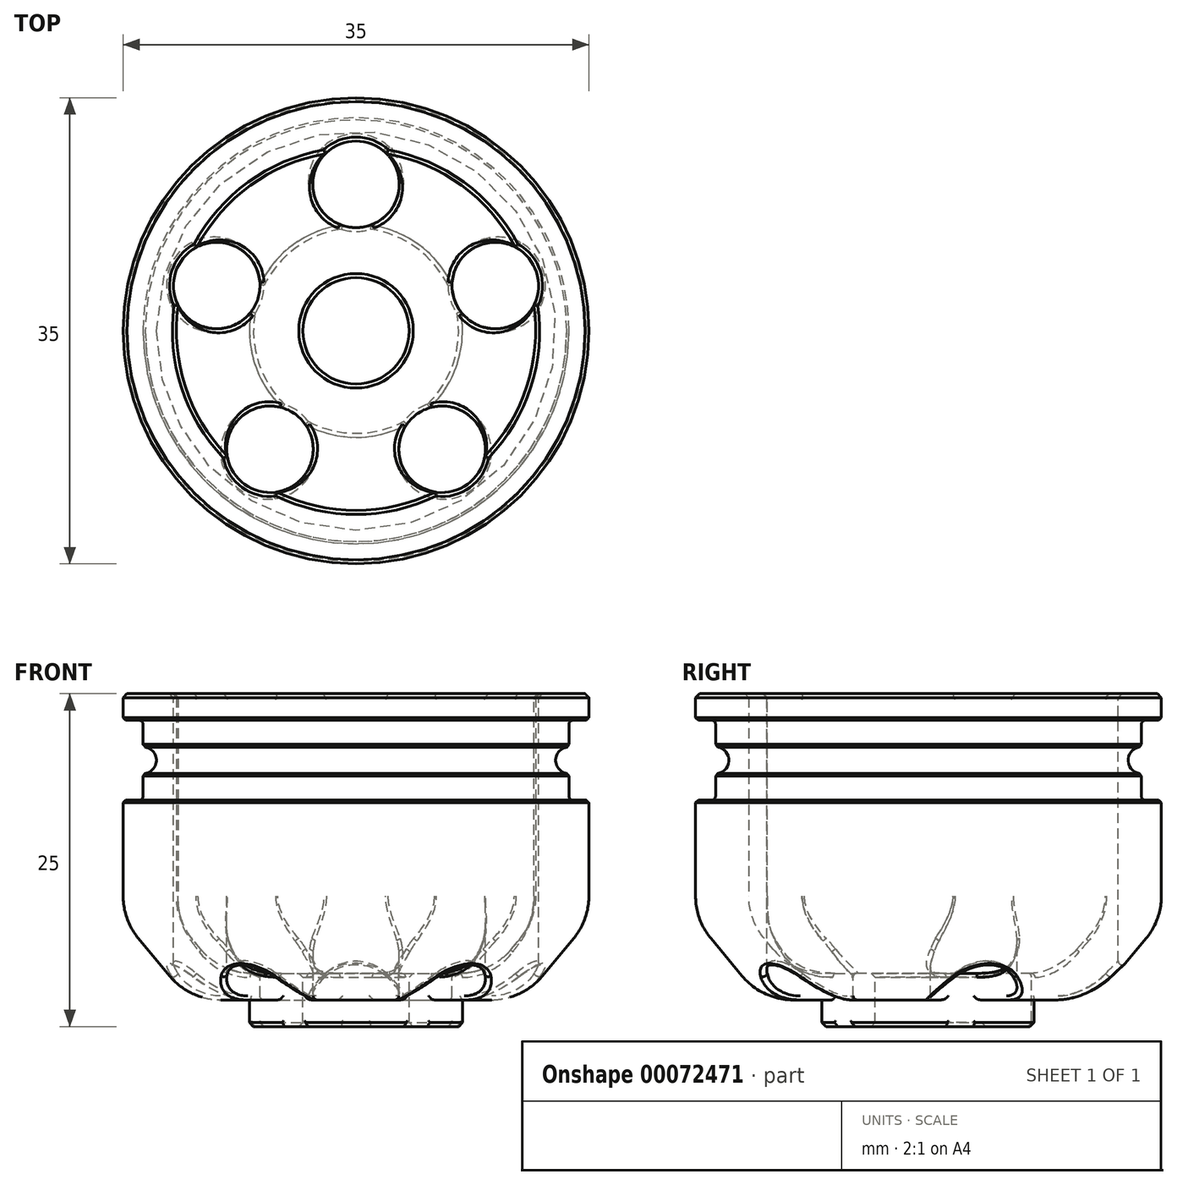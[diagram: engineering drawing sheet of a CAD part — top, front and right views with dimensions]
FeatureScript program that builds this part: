
annotation { "Feature Type Name" : "Feature", "Feature Type Description" : "" }
export const myFeature = defineFeature(function(context is Context, id is Id, definition is map)
    precondition{}
    {
        {
            var Q0;
            Q0=qCreatedBy(makeId("Front.planeOp"),FACE);
            var sketch = newSketch(context, id + "F0", { "sketchPlane" : qUnion([Q0])});
            skLineSegment(sketch, "E0", {"start": v(0, 0) * mm, "end": v(0, 25.98) * mm, "construction": true});
            skLineSegment(sketch, "E1.bottom", {"start": v(0, 0) * mm, "end": v(-8, 0) * mm});
            skLineSegment(sketch, "E1.left", {"start": v(0, 0) * mm, "end": v(0, 2) * mm});
            skLineSegment(sketch, "E1.right", {"start": v(-8, 0) * mm, "end": v(-8, 2) * mm});
            skLineSegment(sketch, "E2.top", {"start": v(0, 4) * mm, "end": v(-10.16, 4) * mm});
            skLineSegment(sketch, "E2.left", {"start": v(0, 2) * mm, "end": v(0, 4) * mm});
            skLineSegment(sketch, "E2.right", {"start": v(-12.5, 2) * mm, "end": v(-12.5, 2) * mm});
            skLineSegment(sketch, "E3", {"start": v(0, 25) * mm, "end": v(-17.5, 25) * mm, "construction": true});
            skLineSegment(sketch, "E4", {"start": v(-17.5, 25) * mm, "end": v(-17.5, 0) * mm, "construction": true});
            skLineSegment(sketch, "E5.bottom", {"start": v(-17.5, 25) * mm, "end": v(-13.5, 25) * mm});
            skLineSegment(sketch, "E5.left", {"start": v(-17.5, 25) * mm, "end": v(-17.5, 23) * mm});
            skLineSegment(sketch, "E5.right", {"start": v(-13.5, 25) * mm, "end": v(-13.5, 8) * mm});
            skLineSegment(sketch, "E6.bottom", {"start": v(-17.5, 23) * mm, "end": v(-16, 23) * mm});
            skLineSegment(sketch, "E6.top", {"start": v(-17.5, 17) * mm, "end": v(-16, 17) * mm});
            skLineSegment(sketch, "E6.right", {"start": v(-16, 23) * mm, "end": v(-16, 21) * mm});
            skLineSegment(sketch, "E7", {"start": v(-17.5, 17) * mm, "end": v(-17.5, 8) * mm});
            skArc(sketch, "E8", {"start": v(-16, 19) * mm, "mid": v(-15, 20) * mm, "end": v(-16, 21) * mm});
            skLineSegment(sketch, "E9", {"start": v(-16, 19) * mm, "end": v(-16, 17) * mm});
            skLineSegment(sketch, "E10", {"start": v(-17.5, 8) * mm, "end": v(-12.5, 2) * mm});
            skLineSegment(sketch, "E11", {"start": v(-13.5, 8) * mm, "end": v(-10.16, 4) * mm});
            skLineSegment(sketch, "E12", {"start": v(-8, 2) * mm, "end": v(-12.5, 2) * mm});
            skSolve(sketch);
        }
        {
            var Q0;
            Q0=makeQuery(id+"F0.imprint","IMPRINT",FACE,{"disambiguationData":[TD([[makeQuery(id+"F0.imprint","IMPRINT",EDGE,{"derivedFrom":sQuery(id+"F0.wireOp",EDGE,"E1.bottom")}),-1.0]])]});
            var Q1;
            Q1=sQuery(id+"F0.wireOp",EDGE,"E0");
            revolve(context, id + "F1", {"entities" : qUnion([Q0]), "axis" : qUnion([Q1]), "revolveType" : RevolveType.FULL});
        }
        {
            var Q0;
            Q0=makeQuery(id+"F1.opRevolve","SWEPT_FACE",FACE,{"disambiguationData":[OSD([sQuery(id+"F0.wireOp",EDGE,"E5.bottom")])]});
            var sketch = newSketch(context, id + "F2", { "sketchPlane" : qUnion([Q0])});
            skCircle(sketch, "E13", {"center": v(0, 0) * mm, "radius": 4 * mm});
            skLineSegment(sketch, "E14", {"start": v(0, 0) * mm, "end": v(0, 11) * mm, "construction": true});
            skCircle(sketch, "E15", {"center": v(0, 0) * mm, "radius": 15 * mm, "construction": true});
            skCircle(sketch, "E16", {"center": v(0, 11) * mm, "radius": 3.25 * mm});
            skCircle(sketch, "E17.1.0", {"center": v(-10.46, 3.4) * mm, "radius": 3.25 * mm});
            skCircle(sketch, "E17.2.0", {"center": v(-6.47, -8.9) * mm, "radius": 3.25 * mm});
            skCircle(sketch, "E17.3.0", {"center": v(6.47, -8.9) * mm, "radius": 3.25 * mm});
            skCircle(sketch, "E17.4.0", {"center": v(10.46, 3.4) * mm, "radius": 3.25 * mm});
            skSolve(sketch);
        }
        {
            var Q0;
            {var subQ0=sQuery(id+"F2.wireOp",EDGE,"E16");var subQ1=makeQuery(id+"F1.opRevolve","SWEPT_EDGE",EDGE,{"disambiguationData":[OSD([sQuery(id+"F0.wireOp",EDGE,"E5.bottom"),sQuery(id+"F0.wireOp",EDGE,"E5.right")])]});var subQ2=makeQuery(id+"F2.imprint","INTERSECT",VERTEX,{"disambiguationData":[OD(0.0)],"derivedFrom":[subQ1,subQ0]});Q0=makeQuery(id+"F2.imprint","IMPRINT",FACE,{"disambiguationData":[TD([[makeQuery(id+"F2.imprint","IMPRINT",EDGE,{"disambiguationData":[TD([[subQ2,-1.0]])],"derivedFrom":subQ0}),1.0]])]});}
            var Q1;
            {var subQ0=sQuery(id+"F2.wireOp",EDGE,"E16");var subQ1=makeQuery(id+"F1.opRevolve","SWEPT_EDGE",EDGE,{"disambiguationData":[OSD([sQuery(id+"F0.wireOp",EDGE,"E5.bottom"),sQuery(id+"F0.wireOp",EDGE,"E5.right")])]});var subQ2=makeQuery(id+"F2.imprint","INTERSECT",VERTEX,{"disambiguationData":[OD(0.0)],"derivedFrom":[subQ1,subQ0]});Q1=makeQuery(id+"F2.imprint","IMPRINT",FACE,{"disambiguationData":[TD([[makeQuery(id+"F2.imprint","IMPRINT",EDGE,{"disambiguationData":[TD([[subQ2,1.0]])],"derivedFrom":subQ0}),1.0]])]});}
            var Q2;
            {var subQ0=sQuery(id+"F2.wireOp",EDGE,"E17.1.0");var subQ1=makeQuery(id+"F1.opRevolve","SWEPT_EDGE",EDGE,{"disambiguationData":[OSD([sQuery(id+"F0.wireOp",EDGE,"E5.bottom"),sQuery(id+"F0.wireOp",EDGE,"E5.right")])]});var subQ2=makeQuery(id+"F2.imprint","INTERSECT",VERTEX,{"disambiguationData":[OD(0.0)],"derivedFrom":[subQ1,subQ0]});Q2=makeQuery(id+"F2.imprint","IMPRINT",FACE,{"disambiguationData":[TD([[makeQuery(id+"F2.imprint","IMPRINT",EDGE,{"disambiguationData":[TD([[subQ2,-1.0]])],"derivedFrom":subQ0}),1.0]])]});}
            var Q3;
            {var subQ0=sQuery(id+"F2.wireOp",EDGE,"E17.1.0");var subQ1=makeQuery(id+"F1.opRevolve","SWEPT_EDGE",EDGE,{"disambiguationData":[OSD([sQuery(id+"F0.wireOp",EDGE,"E5.bottom"),sQuery(id+"F0.wireOp",EDGE,"E5.right")])]});var subQ2=makeQuery(id+"F2.imprint","INTERSECT",VERTEX,{"disambiguationData":[OD(0.0)],"derivedFrom":[subQ1,subQ0]});Q3=makeQuery(id+"F2.imprint","IMPRINT",FACE,{"disambiguationData":[TD([[makeQuery(id+"F2.imprint","IMPRINT",EDGE,{"disambiguationData":[TD([[subQ2,1.0]])],"derivedFrom":subQ0}),1.0]])]});}
            var Q4;
            {var subQ0=sQuery(id+"F2.wireOp",EDGE,"E17.2.0");var subQ1=makeQuery(id+"F1.opRevolve","SWEPT_EDGE",EDGE,{"disambiguationData":[OSD([sQuery(id+"F0.wireOp",EDGE,"E5.bottom"),sQuery(id+"F0.wireOp",EDGE,"E5.right")])]});var subQ2=makeQuery(id+"F2.imprint","INTERSECT",VERTEX,{"disambiguationData":[OD(0.0)],"derivedFrom":[subQ1,subQ0]});Q4=makeQuery(id+"F2.imprint","IMPRINT",FACE,{"disambiguationData":[TD([[makeQuery(id+"F2.imprint","IMPRINT",EDGE,{"disambiguationData":[TD([[subQ2,1.0]])],"derivedFrom":subQ0}),1.0]])]});}
            var Q5;
            {var subQ0=sQuery(id+"F2.wireOp",EDGE,"E17.2.0");var subQ1=makeQuery(id+"F1.opRevolve","SWEPT_EDGE",EDGE,{"disambiguationData":[OSD([sQuery(id+"F0.wireOp",EDGE,"E5.bottom"),sQuery(id+"F0.wireOp",EDGE,"E5.right")])]});var subQ2=makeQuery(id+"F2.imprint","INTERSECT",VERTEX,{"disambiguationData":[OD(0.0)],"derivedFrom":[subQ1,subQ0]});Q5=makeQuery(id+"F2.imprint","IMPRINT",FACE,{"disambiguationData":[TD([[makeQuery(id+"F2.imprint","IMPRINT",EDGE,{"disambiguationData":[TD([[subQ2,-1.0]])],"derivedFrom":subQ0}),1.0]])]});}
            var Q6;
            {var subQ0=sQuery(id+"F2.wireOp",EDGE,"E17.3.0");var subQ1=makeQuery(id+"F1.opRevolve","SWEPT_EDGE",EDGE,{"disambiguationData":[OSD([sQuery(id+"F0.wireOp",EDGE,"E5.bottom"),sQuery(id+"F0.wireOp",EDGE,"E5.right")])]});var subQ2=makeQuery(id+"F2.imprint","INTERSECT",VERTEX,{"disambiguationData":[OD(0.0)],"derivedFrom":[subQ1,subQ0]});Q6=makeQuery(id+"F2.imprint","IMPRINT",FACE,{"disambiguationData":[TD([[makeQuery(id+"F2.imprint","IMPRINT",EDGE,{"disambiguationData":[TD([[subQ2,1.0]])],"derivedFrom":subQ0}),1.0]])]});}
            var Q7;
            {var subQ0=sQuery(id+"F2.wireOp",EDGE,"E17.3.0");var subQ1=makeQuery(id+"F1.opRevolve","SWEPT_EDGE",EDGE,{"disambiguationData":[OSD([sQuery(id+"F0.wireOp",EDGE,"E5.bottom"),sQuery(id+"F0.wireOp",EDGE,"E5.right")])]});var subQ2=makeQuery(id+"F2.imprint","INTERSECT",VERTEX,{"disambiguationData":[OD(0.0)],"derivedFrom":[subQ1,subQ0]});Q7=makeQuery(id+"F2.imprint","IMPRINT",FACE,{"disambiguationData":[TD([[makeQuery(id+"F2.imprint","IMPRINT",EDGE,{"disambiguationData":[TD([[subQ2,-1.0]])],"derivedFrom":subQ0}),1.0]])]});}
            var Q8;
            {var subQ0=sQuery(id+"F2.wireOp",EDGE,"E17.4.0");var subQ1=makeQuery(id+"F1.opRevolve","SWEPT_EDGE",EDGE,{"disambiguationData":[OSD([sQuery(id+"F0.wireOp",EDGE,"E5.bottom"),sQuery(id+"F0.wireOp",EDGE,"E5.right")])]});var subQ2=makeQuery(id+"F2.imprint","INTERSECT",VERTEX,{"disambiguationData":[OD(0.0)],"derivedFrom":[subQ1,subQ0]});Q8=makeQuery(id+"F2.imprint","IMPRINT",FACE,{"disambiguationData":[TD([[makeQuery(id+"F2.imprint","IMPRINT",EDGE,{"disambiguationData":[TD([[subQ2,1.0]])],"derivedFrom":subQ0}),1.0]])]});}
            var Q9;
            {var subQ0=sQuery(id+"F2.wireOp",EDGE,"E17.4.0");var subQ1=makeQuery(id+"F1.opRevolve","SWEPT_EDGE",EDGE,{"disambiguationData":[OSD([sQuery(id+"F0.wireOp",EDGE,"E5.bottom"),sQuery(id+"F0.wireOp",EDGE,"E5.right")])]});var subQ2=makeQuery(id+"F2.imprint","INTERSECT",VERTEX,{"disambiguationData":[OD(0.0)],"derivedFrom":[subQ1,subQ0]});Q9=makeQuery(id+"F2.imprint","IMPRINT",FACE,{"disambiguationData":[TD([[makeQuery(id+"F2.imprint","IMPRINT",EDGE,{"disambiguationData":[TD([[subQ2,-1.0]])],"derivedFrom":subQ0}),1.0]])]});}
            var Q10;
            Q10=makeQuery(id+"F2.imprint","IMPRINT",FACE,{"disambiguationData":[TD([[makeQuery(id+"F2.imprint","IMPRINT",EDGE,{"derivedFrom":sQuery(id+"F2.wireOp",EDGE,"E13")}),1.0]])]});
            extrude(context, id + "F3", {"entities" : qUnion([Q0, Q1, Q2, Q3, Q4, Q5, Q6, Q7, Q8, Q9, Q10]), "operationType" : NewBodyOperationType.REMOVE, "endBound" : BoundingType.THROUGH_ALL, "oppositeDirection" : true, "depth" : 25 * mm});
        }
        {
            var Q0;
            Q0=makeQuery(id+"F1.opRevolve","SWEPT_FACE",FACE,{"disambiguationData":[OSD([sQuery(id+"F0.wireOp",EDGE,"E5.bottom")])]});
            chamfer(context, id + "F4", {"entities" : qUnion([Q0]), "width" : .3 * mm, "tangentPropagation" : true});
        }
        {
            var Q0;
            Q0=makeQuery(id+"F3.boolean.opBoolean","COPY",FACE,{"derivedFrom":makeQuery(id+"F3.opExtrude","SWEPT_FACE",FACE,{"disambiguationData":[OSD([sQuery(id+"F2.wireOp",EDGE,"E13")])]})});
            var Q1;
            Q1=makeQuery(id+"F1.opRevolve","SWEPT_FACE",FACE,{"disambiguationData":[OSD([sQuery(id+"F0.wireOp",EDGE,"E1.bottom")])]});
            chamfer(context, id + "F5", {"entities" : qUnion([Q0, Q1]), "width" : .3 * mm, "tangentPropagation" : true});
        }
        {
            var Q0;
            {var subQ0=sQuery(id+"F0.wireOp",EDGE,"E10");var subQ1=sQuery(id+"F0.wireOp",EDGE,"E12");Q0=makeQuery(id+"F3.boolean.opBoolean","SPLIT",EDGE,{"disambiguationData":[TD([makeQuery(id+"F1.opRevolve","SWEPT_FACE",FACE,{"disambiguationData":[OSD([subQ0])]}),makeQuery(id+"F1.opRevolve","SWEPT_FACE",FACE,{"disambiguationData":[OSD([subQ1])]}),makeQuery(id+"F3.opExtrude","SWEPT_FACE",FACE,{"disambiguationData":[OSD([sQuery(id+"F2.wireOp",EDGE,"E17.2.0")])]}),makeQuery(id+"F3.opExtrude","SWEPT_FACE",FACE,{"disambiguationData":[OSD([sQuery(id+"F2.wireOp",EDGE,"E17.3.0")])]})])],"derivedFrom":makeQuery(id+"F1.opRevolve","SWEPT_EDGE",EDGE,{"disambiguationData":[OSD([subQ0,subQ1])]})});}
            var Q1;
            {var subQ0=sQuery(id+"F0.wireOp",EDGE,"E10");var subQ1=sQuery(id+"F0.wireOp",EDGE,"E12");Q1=makeQuery(id+"F3.boolean.opBoolean","SPLIT",EDGE,{"disambiguationData":[TD([makeQuery(id+"F1.opRevolve","SWEPT_FACE",FACE,{"disambiguationData":[OSD([subQ0])]}),makeQuery(id+"F1.opRevolve","SWEPT_FACE",FACE,{"disambiguationData":[OSD([subQ1])]}),makeQuery(id+"F3.opExtrude","SWEPT_FACE",FACE,{"disambiguationData":[OSD([sQuery(id+"F2.wireOp",EDGE,"E17.3.0")])]}),makeQuery(id+"F3.opExtrude","SWEPT_FACE",FACE,{"disambiguationData":[OSD([sQuery(id+"F2.wireOp",EDGE,"E17.4.0")])]})])],"derivedFrom":makeQuery(id+"F1.opRevolve","SWEPT_EDGE",EDGE,{"disambiguationData":[OSD([subQ0,subQ1])]})});}
            var Q2;
            {var subQ0=sQuery(id+"F0.wireOp",EDGE,"E10");var subQ1=sQuery(id+"F0.wireOp",EDGE,"E12");Q2=makeQuery(id+"F3.boolean.opBoolean","SPLIT",EDGE,{"disambiguationData":[TD([makeQuery(id+"F1.opRevolve","SWEPT_FACE",FACE,{"disambiguationData":[OSD([subQ0])]}),makeQuery(id+"F1.opRevolve","SWEPT_FACE",FACE,{"disambiguationData":[OSD([subQ1])]}),makeQuery(id+"F3.opExtrude","SWEPT_FACE",FACE,{"disambiguationData":[OSD([sQuery(id+"F2.wireOp",EDGE,"E16")])]}),makeQuery(id+"F3.opExtrude","SWEPT_FACE",FACE,{"disambiguationData":[OSD([sQuery(id+"F2.wireOp",EDGE,"E17.4.0")])]})])],"derivedFrom":makeQuery(id+"F1.opRevolve","SWEPT_EDGE",EDGE,{"disambiguationData":[OSD([subQ0,subQ1])]})});}
            var Q3;
            {var subQ0=sQuery(id+"F0.wireOp",EDGE,"E10");var subQ1=sQuery(id+"F0.wireOp",EDGE,"E12");Q3=makeQuery(id+"F3.boolean.opBoolean","SPLIT",EDGE,{"disambiguationData":[TD([makeQuery(id+"F1.opRevolve","SWEPT_FACE",FACE,{"disambiguationData":[OSD([subQ0])]}),makeQuery(id+"F1.opRevolve","SWEPT_FACE",FACE,{"disambiguationData":[OSD([subQ1])]}),makeQuery(id+"F3.opExtrude","SWEPT_FACE",FACE,{"disambiguationData":[OSD([sQuery(id+"F2.wireOp",EDGE,"E16")])]}),makeQuery(id+"F3.opExtrude","SWEPT_FACE",FACE,{"disambiguationData":[OSD([sQuery(id+"F2.wireOp",EDGE,"E17.1.0")])]})])],"derivedFrom":makeQuery(id+"F1.opRevolve","SWEPT_EDGE",EDGE,{"disambiguationData":[OSD([subQ0,subQ1])]})});}
            var Q4;
            {var subQ0=sQuery(id+"F0.wireOp",EDGE,"E10");var subQ1=sQuery(id+"F0.wireOp",EDGE,"E12");Q4=makeQuery(id+"F3.boolean.opBoolean","SPLIT",EDGE,{"disambiguationData":[TD([makeQuery(id+"F1.opRevolve","SWEPT_FACE",FACE,{"disambiguationData":[OSD([subQ0])]}),makeQuery(id+"F1.opRevolve","SWEPT_FACE",FACE,{"disambiguationData":[OSD([subQ1])]}),makeQuery(id+"F3.opExtrude","SWEPT_FACE",FACE,{"disambiguationData":[OSD([sQuery(id+"F2.wireOp",EDGE,"E17.1.0")])]}),makeQuery(id+"F3.opExtrude","SWEPT_FACE",FACE,{"disambiguationData":[OSD([sQuery(id+"F2.wireOp",EDGE,"E17.2.0")])]})])],"derivedFrom":makeQuery(id+"F1.opRevolve","SWEPT_EDGE",EDGE,{"disambiguationData":[OSD([subQ0,subQ1])]})});}
            var Q5;
            {var subQ0=sQuery(id+"F0.wireOp",EDGE,"E2.top");var subQ1=sQuery(id+"F0.wireOp",EDGE,"E11");Q5=makeQuery(id+"F3.boolean.opBoolean","SPLIT",EDGE,{"disambiguationData":[TD([makeQuery(id+"F1.opRevolve","SWEPT_FACE",FACE,{"disambiguationData":[OSD([subQ0])]}),makeQuery(id+"F1.opRevolve","SWEPT_FACE",FACE,{"disambiguationData":[OSD([subQ1])]}),makeQuery(id+"F3.opExtrude","SWEPT_FACE",FACE,{"disambiguationData":[OSD([sQuery(id+"F2.wireOp",EDGE,"E17.2.0")])]}),makeQuery(id+"F3.opExtrude","SWEPT_FACE",FACE,{"disambiguationData":[OSD([sQuery(id+"F2.wireOp",EDGE,"E17.3.0")])]})])],"derivedFrom":makeQuery(id+"F1.opRevolve","SWEPT_EDGE",EDGE,{"disambiguationData":[OSD([subQ0,subQ1])]})});}
            var Q6;
            {var subQ0=sQuery(id+"F0.wireOp",EDGE,"E2.top");var subQ1=sQuery(id+"F0.wireOp",EDGE,"E11");Q6=makeQuery(id+"F3.boolean.opBoolean","SPLIT",EDGE,{"disambiguationData":[TD([makeQuery(id+"F1.opRevolve","SWEPT_FACE",FACE,{"disambiguationData":[OSD([subQ0])]}),makeQuery(id+"F1.opRevolve","SWEPT_FACE",FACE,{"disambiguationData":[OSD([subQ1])]}),makeQuery(id+"F3.opExtrude","SWEPT_FACE",FACE,{"disambiguationData":[OSD([sQuery(id+"F2.wireOp",EDGE,"E17.3.0")])]}),makeQuery(id+"F3.opExtrude","SWEPT_FACE",FACE,{"disambiguationData":[OSD([sQuery(id+"F2.wireOp",EDGE,"E17.4.0")])]})])],"derivedFrom":makeQuery(id+"F1.opRevolve","SWEPT_EDGE",EDGE,{"disambiguationData":[OSD([subQ0,subQ1])]})});}
            var Q7;
            {var subQ0=sQuery(id+"F0.wireOp",EDGE,"E2.top");var subQ1=sQuery(id+"F0.wireOp",EDGE,"E11");Q7=makeQuery(id+"F3.boolean.opBoolean","SPLIT",EDGE,{"disambiguationData":[TD([makeQuery(id+"F1.opRevolve","SWEPT_FACE",FACE,{"disambiguationData":[OSD([subQ0])]}),makeQuery(id+"F1.opRevolve","SWEPT_FACE",FACE,{"disambiguationData":[OSD([subQ1])]}),makeQuery(id+"F3.opExtrude","SWEPT_FACE",FACE,{"disambiguationData":[OSD([sQuery(id+"F2.wireOp",EDGE,"E17.1.0")])]}),makeQuery(id+"F3.opExtrude","SWEPT_FACE",FACE,{"disambiguationData":[OSD([sQuery(id+"F2.wireOp",EDGE,"E17.2.0")])]})])],"derivedFrom":makeQuery(id+"F1.opRevolve","SWEPT_EDGE",EDGE,{"disambiguationData":[OSD([subQ0,subQ1])]})});}
            var Q8;
            {var subQ0=sQuery(id+"F0.wireOp",EDGE,"E2.top");var subQ1=sQuery(id+"F0.wireOp",EDGE,"E11");Q8=makeQuery(id+"F3.boolean.opBoolean","SPLIT",EDGE,{"disambiguationData":[TD([makeQuery(id+"F1.opRevolve","SWEPT_FACE",FACE,{"disambiguationData":[OSD([subQ0])]}),makeQuery(id+"F1.opRevolve","SWEPT_FACE",FACE,{"disambiguationData":[OSD([subQ1])]}),makeQuery(id+"F3.opExtrude","SWEPT_FACE",FACE,{"disambiguationData":[OSD([sQuery(id+"F2.wireOp",EDGE,"E16")])]}),makeQuery(id+"F3.opExtrude","SWEPT_FACE",FACE,{"disambiguationData":[OSD([sQuery(id+"F2.wireOp",EDGE,"E17.1.0")])]})])],"derivedFrom":makeQuery(id+"F1.opRevolve","SWEPT_EDGE",EDGE,{"disambiguationData":[OSD([subQ0,subQ1])]})});}
            var Q9;
            {var subQ0=sQuery(id+"F0.wireOp",EDGE,"E2.top");var subQ1=sQuery(id+"F0.wireOp",EDGE,"E11");Q9=makeQuery(id+"F3.boolean.opBoolean","SPLIT",EDGE,{"disambiguationData":[TD([makeQuery(id+"F1.opRevolve","SWEPT_FACE",FACE,{"disambiguationData":[OSD([subQ0])]}),makeQuery(id+"F1.opRevolve","SWEPT_FACE",FACE,{"disambiguationData":[OSD([subQ1])]}),makeQuery(id+"F3.opExtrude","SWEPT_FACE",FACE,{"disambiguationData":[OSD([sQuery(id+"F2.wireOp",EDGE,"E16")])]}),makeQuery(id+"F3.opExtrude","SWEPT_FACE",FACE,{"disambiguationData":[OSD([sQuery(id+"F2.wireOp",EDGE,"E17.4.0")])]})])],"derivedFrom":makeQuery(id+"F1.opRevolve","SWEPT_EDGE",EDGE,{"disambiguationData":[OSD([subQ0,subQ1])]})});}
            var Q10;
            {var subQ0=sQuery(id+"F0.wireOp",EDGE,"E5.right");var subQ1=sQuery(id+"F0.wireOp",EDGE,"E11");Q10=makeQuery(id+"F3.boolean.opBoolean","SPLIT",EDGE,{"disambiguationData":[TD([makeQuery(id+"F1.opRevolve","SWEPT_FACE",FACE,{"disambiguationData":[OSD([subQ0])]}),makeQuery(id+"F1.opRevolve","SWEPT_FACE",FACE,{"disambiguationData":[OSD([subQ1])]}),makeQuery(id+"F3.opExtrude","SWEPT_FACE",FACE,{"disambiguationData":[OSD([sQuery(id+"F2.wireOp",EDGE,"E17.3.0")])]}),makeQuery(id+"F3.opExtrude","SWEPT_FACE",FACE,{"disambiguationData":[OSD([sQuery(id+"F2.wireOp",EDGE,"E17.4.0")])]})])],"derivedFrom":makeQuery(id+"F1.opRevolve","SWEPT_EDGE",EDGE,{"disambiguationData":[OSD([subQ0,subQ1])]})});}
            var Q11;
            {var subQ0=sQuery(id+"F0.wireOp",EDGE,"E5.right");var subQ1=sQuery(id+"F0.wireOp",EDGE,"E11");Q11=makeQuery(id+"F3.boolean.opBoolean","SPLIT",EDGE,{"disambiguationData":[TD([makeQuery(id+"F1.opRevolve","SWEPT_FACE",FACE,{"disambiguationData":[OSD([subQ0])]}),makeQuery(id+"F1.opRevolve","SWEPT_FACE",FACE,{"disambiguationData":[OSD([subQ1])]}),makeQuery(id+"F3.opExtrude","SWEPT_FACE",FACE,{"disambiguationData":[OSD([sQuery(id+"F2.wireOp",EDGE,"E17.2.0")])]}),makeQuery(id+"F3.opExtrude","SWEPT_FACE",FACE,{"disambiguationData":[OSD([sQuery(id+"F2.wireOp",EDGE,"E17.3.0")])]})])],"derivedFrom":makeQuery(id+"F1.opRevolve","SWEPT_EDGE",EDGE,{"disambiguationData":[OSD([subQ0,subQ1])]})});}
            var Q12;
            {var subQ0=sQuery(id+"F0.wireOp",EDGE,"E5.right");var subQ1=sQuery(id+"F0.wireOp",EDGE,"E11");Q12=makeQuery(id+"F3.boolean.opBoolean","SPLIT",EDGE,{"disambiguationData":[TD([makeQuery(id+"F1.opRevolve","SWEPT_FACE",FACE,{"disambiguationData":[OSD([subQ0])]}),makeQuery(id+"F1.opRevolve","SWEPT_FACE",FACE,{"disambiguationData":[OSD([subQ1])]}),makeQuery(id+"F3.opExtrude","SWEPT_FACE",FACE,{"disambiguationData":[OSD([sQuery(id+"F2.wireOp",EDGE,"E16")])]}),makeQuery(id+"F3.opExtrude","SWEPT_FACE",FACE,{"disambiguationData":[OSD([sQuery(id+"F2.wireOp",EDGE,"E17.4.0")])]})])],"derivedFrom":makeQuery(id+"F1.opRevolve","SWEPT_EDGE",EDGE,{"disambiguationData":[OSD([subQ0,subQ1])]})});}
            var Q13;
            {var subQ0=sQuery(id+"F0.wireOp",EDGE,"E5.right");var subQ1=sQuery(id+"F0.wireOp",EDGE,"E11");Q13=makeQuery(id+"F3.boolean.opBoolean","SPLIT",EDGE,{"disambiguationData":[TD([makeQuery(id+"F1.opRevolve","SWEPT_FACE",FACE,{"disambiguationData":[OSD([subQ0])]}),makeQuery(id+"F1.opRevolve","SWEPT_FACE",FACE,{"disambiguationData":[OSD([subQ1])]}),makeQuery(id+"F3.opExtrude","SWEPT_FACE",FACE,{"disambiguationData":[OSD([sQuery(id+"F2.wireOp",EDGE,"E16")])]}),makeQuery(id+"F3.opExtrude","SWEPT_FACE",FACE,{"disambiguationData":[OSD([sQuery(id+"F2.wireOp",EDGE,"E17.1.0")])]})])],"derivedFrom":makeQuery(id+"F1.opRevolve","SWEPT_EDGE",EDGE,{"disambiguationData":[OSD([subQ0,subQ1])]})});}
            var Q14;
            {var subQ0=sQuery(id+"F0.wireOp",EDGE,"E5.right");var subQ1=sQuery(id+"F0.wireOp",EDGE,"E11");Q14=makeQuery(id+"F3.boolean.opBoolean","SPLIT",EDGE,{"disambiguationData":[TD([makeQuery(id+"F1.opRevolve","SWEPT_FACE",FACE,{"disambiguationData":[OSD([subQ0])]}),makeQuery(id+"F1.opRevolve","SWEPT_FACE",FACE,{"disambiguationData":[OSD([subQ1])]}),makeQuery(id+"F3.opExtrude","SWEPT_FACE",FACE,{"disambiguationData":[OSD([sQuery(id+"F2.wireOp",EDGE,"E17.1.0")])]}),makeQuery(id+"F3.opExtrude","SWEPT_FACE",FACE,{"disambiguationData":[OSD([sQuery(id+"F2.wireOp",EDGE,"E17.2.0")])]})])],"derivedFrom":makeQuery(id+"F1.opRevolve","SWEPT_EDGE",EDGE,{"disambiguationData":[OSD([subQ0,subQ1])]})});}
            var Q15;
            Q15=makeQuery(id+"F1.opRevolve","SWEPT_EDGE",EDGE,{"disambiguationData":[OSD([sQuery(id+"F0.wireOp",EDGE,"E7"),sQuery(id+"F0.wireOp",EDGE,"E10")])]});
            fillet(context, id + "F6", {"entities" : qUnion([Q0, Q1, Q2, Q3, Q4, Q5, Q6, Q7, Q8, Q9, Q10, Q11, Q12, Q13, Q14, Q15]), "radius" : 5 * mm, "tangentPropagation" : true, "allowEdgeOverflow" : false});
        }
        {
            var Q0;
            Q0=makeQuery(id+"F3.boolean.opBoolean","COPY",FACE,{"derivedFrom":makeQuery(id+"F3.opExtrude","SWEPT_FACE",FACE,{"disambiguationData":[OSD([sQuery(id+"F2.wireOp",EDGE,"E17.1.0")])]})});
            var Q1;
            Q1=makeQuery(id+"F3.boolean.opBoolean","COPY",FACE,{"derivedFrom":makeQuery(id+"F3.opExtrude","SWEPT_FACE",FACE,{"disambiguationData":[OSD([sQuery(id+"F2.wireOp",EDGE,"E17.2.0")])]})});
            var Q2;
            Q2=makeQuery(id+"F3.boolean.opBoolean","COPY",FACE,{"derivedFrom":makeQuery(id+"F3.opExtrude","SWEPT_FACE",FACE,{"disambiguationData":[OSD([sQuery(id+"F2.wireOp",EDGE,"E16")])]})});
            var Q3;
            Q3=makeQuery(id+"F3.boolean.opBoolean","COPY",FACE,{"derivedFrom":makeQuery(id+"F3.opExtrude","SWEPT_FACE",FACE,{"disambiguationData":[OSD([sQuery(id+"F2.wireOp",EDGE,"E17.4.0")])]})});
            var Q4;
            Q4=makeQuery(id+"F3.boolean.opBoolean","COPY",FACE,{"derivedFrom":makeQuery(id+"F3.opExtrude","SWEPT_FACE",FACE,{"disambiguationData":[OSD([sQuery(id+"F2.wireOp",EDGE,"E17.3.0")])]})});
            fillet(context, id + "F7", {"entities" : qUnion([Q0, Q1, Q2, Q3, Q4]), "radius" : .3 * mm, "tangentPropagation" : true, "allowEdgeOverflow" : false});
        }
        {
            var Q0;
            Q0=makeQuery(id+"F1.opRevolve","SWEPT_EDGE",EDGE,{"disambiguationData":[OSD([sQuery(id+"F0.wireOp",EDGE,"E6.top"),sQuery(id+"F0.wireOp",EDGE,"E7")])]});
            var Q1;
            Q1=makeQuery(id+"F1.opRevolve","SWEPT_EDGE",EDGE,{"disambiguationData":[OSD([sQuery(id+"F0.wireOp",EDGE,"E5.left"),sQuery(id+"F0.wireOp",EDGE,"E6.bottom")])]});
            var Q2;
            Q2=makeQuery(id+"F1.opRevolve","SWEPT_EDGE",EDGE,{"disambiguationData":[OSD([sQuery(id+"F0.wireOp",EDGE,"E8"),sQuery(id+"F0.wireOp",EDGE,"E9")])]});
            var Q3;
            Q3=makeQuery(id+"F1.opRevolve","SWEPT_EDGE",EDGE,{"disambiguationData":[OSD([sQuery(id+"F0.wireOp",EDGE,"E6.right"),sQuery(id+"F0.wireOp",EDGE,"E8")])]});
            chamfer(context, id + "F8", {"entities" : qUnion([Q0, Q1, Q2, Q3]), "width" : .2 * mm, "tangentPropagation" : true});
        }
        {
            var Q0;
            Q0=makeQuery(id+"F1.opRevolve","SWEPT_EDGE",EDGE,{"disambiguationData":[OSD([sQuery(id+"F0.wireOp",EDGE,"E6.top"),sQuery(id+"F0.wireOp",EDGE,"E9")])]});
            var Q1;
            Q1=makeQuery(id+"F1.opRevolve","SWEPT_EDGE",EDGE,{"disambiguationData":[OSD([sQuery(id+"F0.wireOp",EDGE,"E6.bottom"),sQuery(id+"F0.wireOp",EDGE,"E6.right")])]});
            fillet(context, id + "F9", {"entities" : qUnion([Q0, Q1]), "radius" : .3 * mm, "tangentPropagation" : true, "allowEdgeOverflow" : false});
        }
    });
